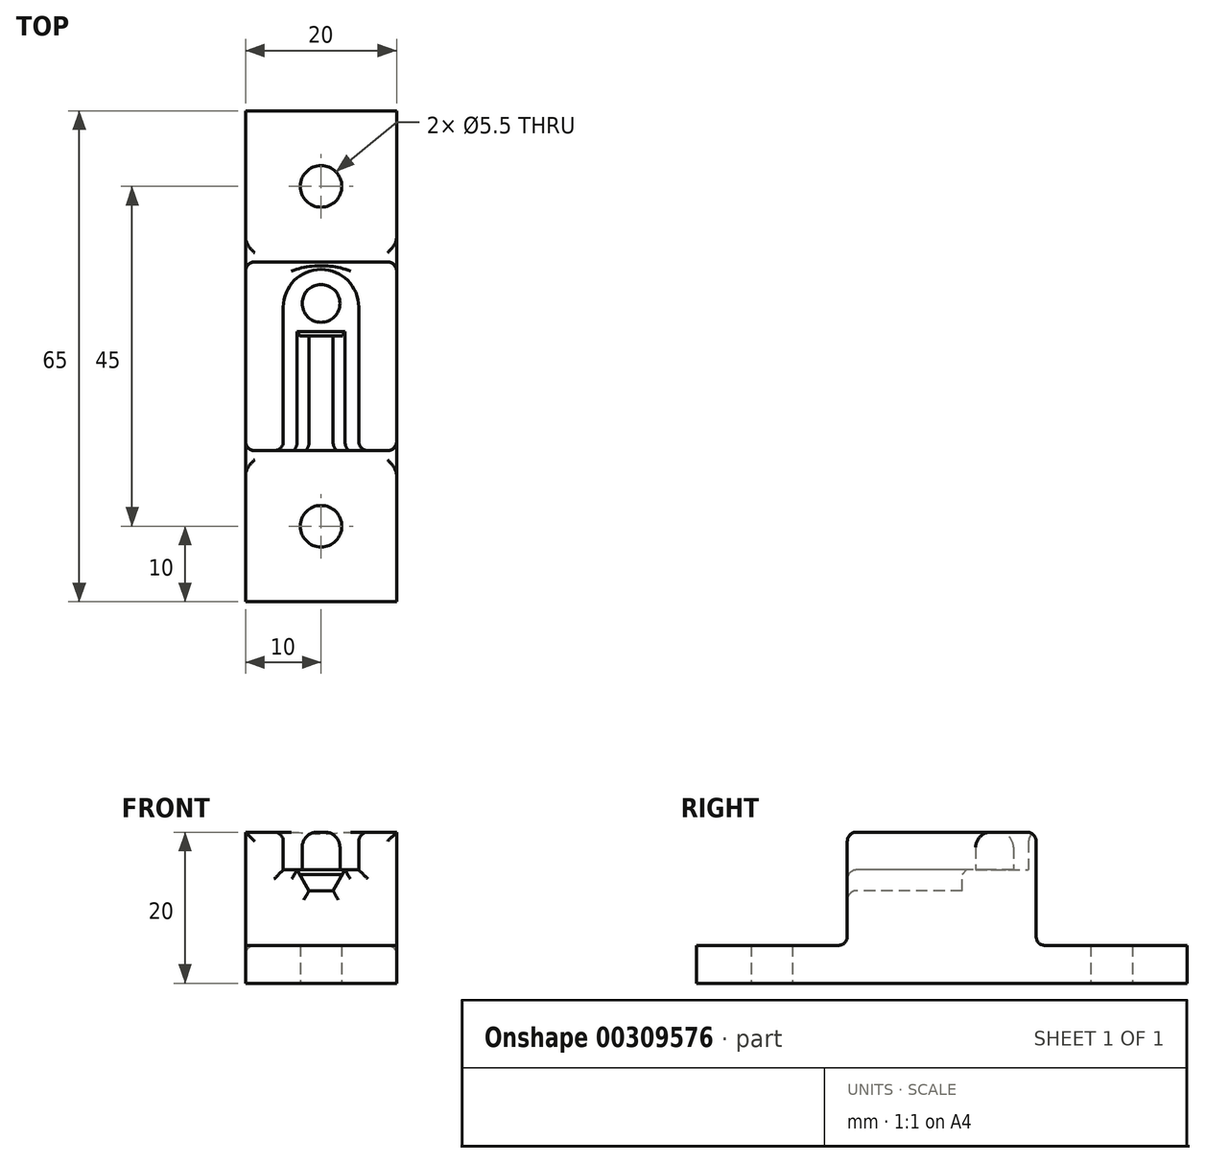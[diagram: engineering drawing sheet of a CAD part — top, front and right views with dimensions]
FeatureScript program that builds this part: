
annotation { "Feature Type Name" : "Feature", "Feature Type Description" : "" }
export const myFeature = defineFeature(function(context is Context, id is Id, definition is map)
    precondition{}
    {
        {
            var Q0;
            Q0=qCreatedBy(makeId("Top.planeOp"),FACE);
            var sketch = newSketch(context, id + "F0", { "sketchPlane" : qUnion([Q0])});
            skLineSegment(sketch, "E0.bottom", {"start": v(-10, 32.5) * mm, "end": v(10, 32.5) * mm});
            skLineSegment(sketch, "E0.top", {"start": v(-10, -32.5) * mm, "end": v(10, -32.5) * mm});
            skLineSegment(sketch, "E0.left", {"start": v(-10, 32.5) * mm, "end": v(-10, -32.5) * mm});
            skLineSegment(sketch, "E0.right", {"start": v(10, 32.5) * mm, "end": v(10, -32.5) * mm});
            skLineSegment(sketch, "E1", {"start": v(0, 0) * mm, "end": v(0, 32.5) * mm, "construction": true});
            skPoint(sketch, "E2", {"position": v(0, 22.5) * mm});
            skPoint(sketch, "E3", {"position": v(0, -22.5) * mm});
            skLineSegment(sketch, "E4", {"start": v(0, 0) * mm, "end": v(10, 0) * mm, "construction": true});
            skLineSegment(sketch, "E5.bottom", {"start": v(-10, 12.5) * mm, "end": v(10, 12.5) * mm});
            skLineSegment(sketch, "E5.top", {"start": v(-10, -12.5) * mm, "end": v(10, -12.5) * mm});
            skLineSegment(sketch, "E5.left", {"start": v(-10, 12.5) * mm, "end": v(-10, -12.5) * mm});
            skLineSegment(sketch, "E5.right", {"start": v(10, 12.5) * mm, "end": v(10, -12.5) * mm});
            skSolve(sketch);
        }
        {
            var Q0;
            {var subQ0=sQuery(id+"F0.wireOp",EDGE,"E0.bottom");Q0=makeQuery(id+"F0.imprint","IMPRINT",FACE,{"disambiguationData":[TD([[makeQuery(id+"F0.imprint","IMPRINT",EDGE,{"derivedFrom":subQ0}),-1.0]])]});}
            var Q1;
            {var subQ0=sQuery(id+"F0.wireOp",EDGE,"E0.top");Q1=makeQuery(id+"F0.imprint","IMPRINT",FACE,{"disambiguationData":[TD([[makeQuery(id+"F0.imprint","IMPRINT",EDGE,{"derivedFrom":subQ0}),1.0]])]});}
            var Q2;
            Q2=makeQuery(id+"F0.imprint","IMPRINT",FACE,{"disambiguationData":[TD([[makeQuery(id+"F0.imprint","IMPRINT",EDGE,{"derivedFrom":sQuery(id+"F0.wireOp",EDGE,"E5.bottom")}),-1.0]])]});
            extrude(context, id + "F1", {"entities" : qUnion([Q0, Q1, Q2]), "depth" : 5 * mm, "offsetDistance" : 25 * mm});
        }
        {
            var Q0;
            Q0=makeQuery(id+"F0.imprint","IMPRINT",FACE,{"disambiguationData":[TD([[makeQuery(id+"F0.imprint","IMPRINT",EDGE,{"derivedFrom":sQuery(id+"F0.wireOp",EDGE,"E5.bottom")}),-1.0]])]});
            extrude(context, id + "F2", {"entities" : qUnion([Q0]), "operationType" : NewBodyOperationType.ADD, "depth" : 15 * mm, "offsetDistance" : 25 * mm});
        }
        {
            var Q0;
            Q0=makeQuery(id+"F2.opExtrude","CAP_FACE",FACE,{"disambiguationData":[OSD([sQuery(id+"F0.wireOp",EDGE,"E5.bottom"),sQuery(id+"F0.wireOp",EDGE,"E5.top"),sQuery(id+"F0.wireOp",EDGE,"E5.left"),sQuery(id+"F0.wireOp",EDGE,"E5.right")])],"isStart":false});
            var sketch = newSketch(context, id + "F3", { "sketchPlane" : qUnion([Q0])});
            skLineSegment(sketch, "E6.0", {"start": v(0, 0) * mm, "end": v(0, 32.5) * mm});
            skLineSegment(sketch, "E7.0", {"start": v(0, 0) * mm, "end": v(10, 0) * mm});
            skPoint(sketch, "E8", {"position": v(0, 7) * mm});
            skCircle(sketch, "E9", {"center": v(0, 7) * mm, "radius": 2.5 * mm});
            skLineSegment(sketch, "E10", {"start": v(-5, -12.5) * mm, "end": v(-5, 6.5) * mm});
            skArc(sketch, "E11", {"start": v(5, 6.5) * mm, "mid": v(0, 11.5) * mm, "end": v(-5, 6.5) * mm});
            skLineSegment(sketch, "E12", {"start": v(5, 6.5) * mm, "end": v(5, -12.5) * mm});
            skLineSegment(sketch, "E13", {"start": v(-5, -12.5) * mm, "end": v(5, -12.5) * mm});
            skSolve(sketch);
        }
        {
            var Q0;
            {var subQ0=sQuery(id+"F3.wireOp",EDGE,"E9");var subQ1=sQuery(id+"F3.wireOp",EDGE,"E6.0");var subQ2=makeQuery(id+"F3.imprint","INTERSECT",VERTEX,{"disambiguationData":[OD(0.0)],"derivedFrom":[subQ1,subQ0]});Q0=makeQuery(id+"F3.imprint","IMPRINT",FACE,{"disambiguationData":[TD([[makeQuery(id+"F3.imprint","IMPRINT",EDGE,{"disambiguationData":[TD([[subQ2,-1.0]])],"derivedFrom":subQ1}),1.0]])]});}
            var Q1;
            {var subQ0=sQuery(id+"F3.wireOp",EDGE,"E9");var subQ1=sQuery(id+"F3.wireOp",EDGE,"E6.0");var subQ2=makeQuery(id+"F3.imprint","INTERSECT",VERTEX,{"disambiguationData":[OD(0.0)],"derivedFrom":[subQ1,subQ0]});Q1=makeQuery(id+"F3.imprint","IMPRINT",FACE,{"disambiguationData":[TD([[makeQuery(id+"F3.imprint","IMPRINT",EDGE,{"disambiguationData":[TD([[subQ2,-1.0]])],"derivedFrom":subQ1}),-1.0]])]});}
            extrude(context, id + "F4", {"entities" : qUnion([Q0, Q1]), "operationType" : NewBodyOperationType.ADD, "depth" : 5 * mm, "offsetDistance" : 25 * mm});
        }
        {
            var Q0;
            Q0=makeQuery(id+"F4.opExtrude","CAP_EDGE",EDGE,{"disambiguationData":[OSD([sQuery(id+"F3.wireOp",EDGE,"E9")])],"isStart":false});
            fillet(context, id + "F5", {"entities" : qUnion([Q0]), "radius" : 2 * mm, "tangentPropagation" : true, "allowEdgeOverflow" : false});
        }
        {
            var Q0;
            {var subQ6=sQuery(id+"F3.wireOp",EDGE,"E10");Q0=makeQuery(id+"F3.imprint","IMPRINT",FACE,{"disambiguationData":[TD([[makeQuery(id+"F3.imprint","IMPRINT",EDGE,{"derivedFrom":subQ6}),1.0]])]});}
            var Q1;
            {var subQ1=sQuery(id+"F3.wireOp",EDGE,"E11");var subQ5=sQuery(id+"F3.wireOp",EDGE,"E6.0");var subQ6=makeQuery(id+"F3.imprint","INTERSECT",VERTEX,{"derivedFrom":[subQ5,subQ1]});Q1=makeQuery(id+"F3.imprint","IMPRINT",FACE,{"disambiguationData":[TD([[makeQuery(id+"F3.imprint","IMPRINT",EDGE,{"disambiguationData":[TD([[subQ6,-1.0]])],"derivedFrom":subQ5}),-1.0]])]});}
            var Q2;
            {var subQ0=sQuery(id+"F3.wireOp",EDGE,"E7.0");var subQ1=makeQuery(id+"F2.opExtrude","CAP_EDGE",EDGE,{"disambiguationData":[OSD([sQuery(id+"F0.wireOp",EDGE,"E5.right")])],"isStart":false});var subQ2=makeQuery(id+"F3.imprint","INTERSECT",VERTEX,{"derivedFrom":[subQ1,subQ0]});Q2=makeQuery(id+"F3.imprint","IMPRINT",FACE,{"disambiguationData":[TD([[makeQuery(id+"F3.imprint","IMPRINT",EDGE,{"disambiguationData":[TD([[subQ2,1.0]])],"derivedFrom":subQ0}),-1.0]])]});}
            extrude(context, id + "F6", {"entities" : qUnion([Q0, Q1, Q2]), "operationType" : NewBodyOperationType.ADD, "depth" : 5 * mm, "offsetDistance" : 25 * mm});
        }
        {
            var Q0;
            {var subQ0=sQuery(id+"F0.wireOp",EDGE,"E5.top");var subQ1=makeQuery(id+"F2.opExtrude","CAP_EDGE",EDGE,{"disambiguationData":[OSD([subQ0])],"isStart":false});Q0=makeQuery(id+"F6.boolean.opBoolean","MERGE",FACE,{"derivedFrom":[makeQuery(id+"F2.opExtrude","SWEPT_FACE",FACE,{"disambiguationData":[OSD([subQ0])]}),makeQuery(id+"F6.opExtrude","SWEPT_FACE",FACE,{"disambiguationData":[OSD([subQ0]),TDD([makeQuery(id+"F3.imprint","IMPRINT",EDGE,{"disambiguationData":[TD([[makeQuery(id+"F3.imprint","INTERSECT",VERTEX,{"derivedFrom":[subQ1,makeQuery(id+"F2.opExtrude","CAP_EDGE",EDGE,{"disambiguationData":[OSD([sQuery(id+"F0.wireOp",EDGE,"E5.left")])],"isStart":false})]}),-1.0]])],"derivedFrom":subQ1})])]}),makeQuery(id+"F6.opExtrude","SWEPT_FACE",FACE,{"disambiguationData":[OSD([subQ0]),TDD([makeQuery(id+"F3.imprint","IMPRINT",EDGE,{"disambiguationData":[TD([[makeQuery(id+"F3.imprint","INTERSECT",VERTEX,{"derivedFrom":[subQ1,makeQuery(id+"F2.opExtrude","CAP_EDGE",EDGE,{"disambiguationData":[OSD([sQuery(id+"F0.wireOp",EDGE,"E5.right")])],"isStart":false})]}),1.0]])],"derivedFrom":subQ1})])]})]});}
            var sketch = newSketch(context, id + "F7", { "sketchPlane" : qUnion([Q0])});
            skLineSegment(sketch, "E14.0", {"start": v(-5, 15) * mm, "end": v(5, 15) * mm});
            skCircle(sketch, "E15.cCircle", {"center": v(0, 15) * mm, "radius": 2.75 * mm, "construction": true});
            skLineSegment(sketch, "E15.0", {"start": v(1.59, 12.25) * mm, "end": v(-1.59, 12.25) * mm});
            skLineSegment(sketch, "E15.1", {"start": v(-1.59, 12.25) * mm, "end": v(-3.18, 15) * mm});
            skLineSegment(sketch, "E15.2", {"start": v(-3.18, 15) * mm, "end": v(-1.59, 17.75) * mm});
            skLineSegment(sketch, "E15.3", {"start": v(-1.59, 17.75) * mm, "end": v(1.59, 17.75) * mm});
            skLineSegment(sketch, "E15.4", {"start": v(1.59, 17.75) * mm, "end": v(3.18, 15) * mm});
            skLineSegment(sketch, "E15.5", {"start": v(3.18, 15) * mm, "end": v(1.59, 12.25) * mm});
            skPoint(sketch, "E15.0.midPoint", {"position": v(0, 12.25) * mm});
            skSolve(sketch);
        }
        {
            var Q0;
            {var subQ0=sQuery(id+"F7.wireOp",EDGE,"E15.2");Q0=makeQuery(id+"F7.imprint","IMPRINT",FACE,{"disambiguationData":[TD([[makeQuery(id+"F7.imprint","IMPRINT",EDGE,{"derivedFrom":subQ0}),-1.0]])]});}
            var Q1;
            Q1=makeQuery(id+"F7.imprint","IMPRINT",FACE,{"disambiguationData":[TD([[makeQuery(id+"F7.imprint","IMPRINT",EDGE,{"derivedFrom":sQuery(id+"F7.wireOp",EDGE,"E15.0")}),-1.0]])]});
            extrude(context, id + "F8", {"entities" : qUnion([Q0, Q1]), "operationType" : NewBodyOperationType.REMOVE, "oppositeDirection" : true, "depth" : 15.2 * mm, "offsetDistance" : 25 * mm});
        }
        {
            var Q0;
            Q0=makeQuery(id+"F8.boolean.opBoolean","INTERSECT",EDGE,{"derivedFrom":[makeQuery(id+"F2.opExtrude","CAP_FACE",FACE,{"disambiguationData":[OSD([sQuery(id+"F0.wireOp",EDGE,"E5.bottom"),sQuery(id+"F0.wireOp",EDGE,"E5.top"),sQuery(id+"F0.wireOp",EDGE,"E5.left"),sQuery(id+"F0.wireOp",EDGE,"E5.right")])],"isStart":false}),makeQuery(id+"F8.opExtrude","CAP_FACE",FACE,{"disambiguationData":[OSD([sQuery(id+"F7.wireOp",EDGE,"E15.0"),sQuery(id+"F7.wireOp",EDGE,"E15.1"),sQuery(id+"F7.wireOp",EDGE,"E15.2"),sQuery(id+"F7.wireOp",EDGE,"E15.3"),sQuery(id+"F7.wireOp",EDGE,"E15.4"),sQuery(id+"F7.wireOp",EDGE,"E15.5")])],"isStart":false})]});
            var Q1;
            Q1=makeQuery(id+"F8.boolean.opBoolean","COPY",EDGE,{"derivedFrom":makeQuery(id+"F8.opExtrude","SWEPT_EDGE",EDGE,{"disambiguationData":[OSD([sQuery(id+"F7.wireOp",EDGE,"E14.0"),sQuery(id+"F7.wireOp",EDGE,"E15.4"),sQuery(id+"F7.wireOp",EDGE,"E15.5")])]})});
            var Q2;
            Q2=makeQuery(id+"F8.boolean.opBoolean","COPY",EDGE,{"derivedFrom":makeQuery(id+"F8.opExtrude","SWEPT_EDGE",EDGE,{"disambiguationData":[OSD([sQuery(id+"F7.wireOp",EDGE,"E14.0"),sQuery(id+"F7.wireOp",EDGE,"E15.1"),sQuery(id+"F7.wireOp",EDGE,"E15.2")])]})});
            chamfer(context, id + "F9", {"entities" : qUnion([Q0, Q1, Q2]), "width" : 0.6 * mm, "tangentPropagation" : true});
        }
        {
            var Q0;
            Q0=makeQuery(id+"F6.opExtrude","CAP_EDGE",EDGE,{"disambiguationData":[OSD([sQuery(id+"F3.wireOp",EDGE,"E12")])],"isStart":false});
            var Q1;
            Q1=makeQuery(id+"F6.opExtrude","CAP_EDGE",EDGE,{"disambiguationData":[OSD([sQuery(id+"F3.wireOp",EDGE,"E11")])],"isStart":false});
            var Q2;
            Q2=makeQuery(id+"F6.opExtrude","CAP_EDGE",EDGE,{"disambiguationData":[OSD([sQuery(id+"F3.wireOp",EDGE,"E10")])],"isStart":false});
            var Q3;
            Q3=makeQuery(id+"F6.opExtrude","CAP_EDGE",EDGE,{"disambiguationData":[OSD([sQuery(id+"F0.wireOp",EDGE,"E5.bottom")])],"isStart":false});
            var Q4;
            Q4=makeQuery(id+"F6.opExtrude","CAP_EDGE",EDGE,{"disambiguationData":[OSD([sQuery(id+"F0.wireOp",EDGE,"E5.left")])],"isStart":false});
            var Q5;
            Q5=makeQuery(id+"F6.opExtrude","CAP_EDGE",EDGE,{"disambiguationData":[OSD([sQuery(id+"F0.wireOp",EDGE,"E5.right")])],"isStart":false});
            var Q6;
            {var subQ0=sQuery(id+"F0.wireOp",EDGE,"E5.top");var subQ1=makeQuery(id+"F2.opExtrude","CAP_EDGE",EDGE,{"disambiguationData":[OSD([subQ0])],"isStart":false});Q6=makeQuery(id+"F6.boolean.opBoolean","MERGE",FACE,{"derivedFrom":[makeQuery(id+"F2.opExtrude","SWEPT_FACE",FACE,{"disambiguationData":[OSD([subQ0])]}),makeQuery(id+"F6.opExtrude","SWEPT_FACE",FACE,{"disambiguationData":[OSD([subQ0]),TDD([makeQuery(id+"F3.imprint","IMPRINT",EDGE,{"disambiguationData":[TD([[makeQuery(id+"F3.imprint","INTERSECT",VERTEX,{"derivedFrom":[subQ1,makeQuery(id+"F2.opExtrude","CAP_EDGE",EDGE,{"disambiguationData":[OSD([sQuery(id+"F0.wireOp",EDGE,"E5.left")])],"isStart":false})]}),-1.0]])],"derivedFrom":subQ1})])]}),makeQuery(id+"F6.opExtrude","SWEPT_FACE",FACE,{"disambiguationData":[OSD([subQ0]),TDD([makeQuery(id+"F3.imprint","IMPRINT",EDGE,{"disambiguationData":[TD([[makeQuery(id+"F3.imprint","INTERSECT",VERTEX,{"derivedFrom":[subQ1,makeQuery(id+"F2.opExtrude","CAP_EDGE",EDGE,{"disambiguationData":[OSD([sQuery(id+"F0.wireOp",EDGE,"E5.right")])],"isStart":false})]}),1.0]])],"derivedFrom":subQ1})])]})]});}
            var Q7;
            {var subQ0=sQuery(id+"F0.wireOp",EDGE,"E5.bottom");Q7=makeQuery(id+"F6.boolean.opBoolean","MERGE",FACE,{"derivedFrom":[makeQuery(id+"F2.opExtrude","SWEPT_FACE",FACE,{"disambiguationData":[OSD([subQ0])]}),makeQuery(id+"F6.opExtrude","SWEPT_FACE",FACE,{"disambiguationData":[OSD([subQ0])]})]});}
            fillet(context, id + "F10", {"entities" : qUnion([Q0, Q1, Q2, Q3, Q4, Q5, Q6, Q7]), "radius" : 1.2 * mm, "tangentPropagation" : true, "allowEdgeOverflow" : false});
        }
        {
            var Q0;
            Q0=sQuery(id+"F0.wireOp",VERTEX,"E2");
            var Q1;
            Q1=sQuery(id+"F0.wireOp",VERTEX,"E3");
            var Q2;
            Q2=makeQuery(id+"F1.opExtrude","SWEPT_BODY",BODY,{"disambiguationData":[OSD([sQuery(id+"F0.wireOp",EDGE,"E0.bottom"),sQuery(id+"F0.wireOp",EDGE,"E0.top"),sQuery(id+"F0.wireOp",EDGE,"E0.left"),sQuery(id+"F0.wireOp",EDGE,"E0.right"),sQuery(id+"F0.wireOp",EDGE,"E5.left"),sQuery(id+"F0.wireOp",EDGE,"E5.right")])]});
            hole(context, id + "F11", {"style" : HoleStyle.SIMPLE, "endStyle" : HoleEndStyle.THROUGH, "oppositeDirection" : true, "standardTappedOrClearance" : lookupTablePath({ "standard" : "ISO", "fit" : "Normal", "size" : "M5", "type" : "Clearance" }), "standardBlindInLast" : lookupTablePath({ "fit" : "Standard", "standard" : "ISO", "size" : "M5", "type" : "Clearance" }), "holeDiameter" : 5.5 * mm, "majorDiameter" : 5 * mm, "isTappedThrough" : true, "tappedDepth" : 12 * mm, "tapClearance" : 3, "startFromSketch" : true, "locations" : qUnion([Q0, Q1]), "scope" : qUnion([Q2])});
        }
    });
